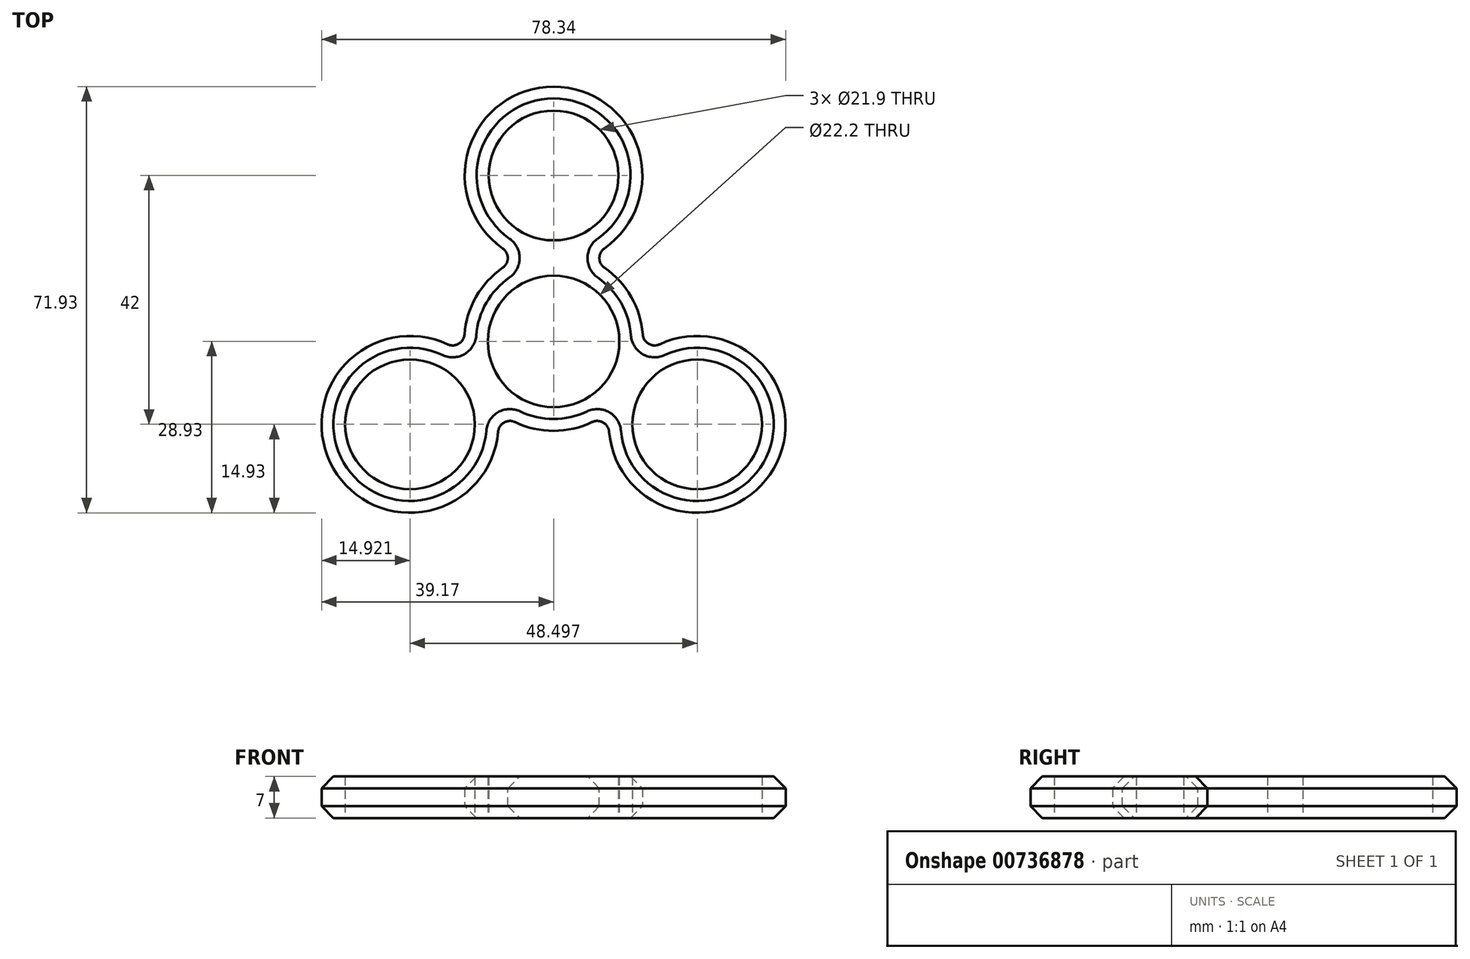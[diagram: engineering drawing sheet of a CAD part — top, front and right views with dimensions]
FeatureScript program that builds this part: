
annotation { "Feature Type Name" : "Feature", "Feature Type Description" : "" }
export const myFeature = defineFeature(function(context is Context, id is Id, definition is map)
    precondition{}
    {
        {
            var Q0;
            Q0=qCreatedBy(makeId("Top.planeOp"),FACE);
            var sketch = newSketch(context, id + "F0", { "sketchPlane" : qUnion([Q0])});
            skLineSegment(sketch, "E0", {"start": v(0, 0) * mm, "end": v(0, 28) * mm, "construction": true});
            skCircle(sketch, "E1", {"center": v(0, 28) * mm, "radius": 10.95 * mm});
            skArc(sketch, "E2", {"start": v(5.52, 14.05) * mm, "mid": v(0, 43) * mm, "end": v(-5.52, 14.05) * mm});
            skCircle(sketch, "E3", {"center": v(0, 0) * mm, "radius": 11.1 * mm});
            skArc(sketch, "E4", {"start": v(-9.5, -11.74) * mm, "mid": v(0, -15.1) * mm, "end": v(9.5, -11.74) * mm});
            skArc(sketch, "E5.1.2", {"start": v(-14.92, -2.35) * mm, "mid": v(-37.17, -21.46) * mm, "end": v(-9.5, -11.74) * mm});
            skCircle(sketch, "E5.1.3", {"center": v(-24.25, -14) * mm, "radius": 10.95 * mm});
            skArc(sketch, "E5.2.2", {"start": v(9.5, -11.74) * mm, "mid": v(37.17, -21.46) * mm, "end": v(14.92, -2.35) * mm});
            skCircle(sketch, "E5.2.3", {"center": v(24.25, -14) * mm, "radius": 10.95 * mm});
            skArc(sketch, "E6.trimOffspring", {"start": v(14.92, -2.35) * mm, "mid": v(13.1, 7.5) * mm, "end": v(5.52, 14.05) * mm});
            skArc(sketch, "E7.trimOffspring", {"start": v(-5.52, 14.05) * mm, "mid": v(-13.1, 7.5) * mm, "end": v(-14.92, -2.35) * mm});
            skLineSegment(sketch, "E8", {"start": v(0, 0) * mm, "end": v(-24.25, -14) * mm, "construction": true});
            skLineSegment(sketch, "E9", {"start": v(0, 0) * mm, "end": v(24.25, -14) * mm, "construction": true});
            skSolve(sketch);
        }
        {
            var Q0;
            Q0=qSketchRegion(id+"F0",true);
            extrude(context, id + "F1", {"entities" : qUnion([Q0]), "depth" : 7 * mm, "offsetDistance" : 25 * mm});
        }
        {
            var Q0;
            Q0=makeQuery(id+"F1.opExtrude","SWEPT_EDGE",EDGE,{"disambiguationData":[OSD([sQuery(id+"F0.wireOp",EDGE,"E4"),sQuery(id+"F0.wireOp",EDGE,"E5.1.2")])]});
            var Q1;
            Q1=makeQuery(id+"F1.opExtrude","SWEPT_EDGE",EDGE,{"disambiguationData":[OSD([sQuery(id+"F0.wireOp",EDGE,"E4"),sQuery(id+"F0.wireOp",EDGE,"E5.2.2")])]});
            var Q2;
            Q2=makeQuery(id+"F1.opExtrude","SWEPT_EDGE",EDGE,{"disambiguationData":[OSD([sQuery(id+"F0.wireOp",EDGE,"E5.2.2"),sQuery(id+"F0.wireOp",EDGE,"E6.trimOffspring")])]});
            var Q3;
            Q3=makeQuery(id+"F1.opExtrude","SWEPT_EDGE",EDGE,{"disambiguationData":[OSD([sQuery(id+"F0.wireOp",EDGE,"E2"),sQuery(id+"F0.wireOp",EDGE,"E6.trimOffspring")])]});
            var Q4;
            Q4=makeQuery(id+"F1.opExtrude","SWEPT_EDGE",EDGE,{"disambiguationData":[OSD([sQuery(id+"F0.wireOp",EDGE,"E2"),sQuery(id+"F0.wireOp",EDGE,"E7.trimOffspring")])]});
            var Q5;
            Q5=makeQuery(id+"F1.opExtrude","SWEPT_EDGE",EDGE,{"disambiguationData":[OSD([sQuery(id+"F0.wireOp",EDGE,"E5.1.2"),sQuery(id+"F0.wireOp",EDGE,"E7.trimOffspring")])]});
            fillet(context, id + "F2", {"entities" : qUnion([Q0, Q1, Q2, Q3, Q4, Q5]), "radius" : 2 * mm, "tangentPropagation" : true, "allowEdgeOverflow" : false});
        }
        {
            var Q0;
            Q0=makeQuery(id+"F1.opExtrude","CAP_EDGE",EDGE,{"disambiguationData":[OSD([sQuery(id+"F0.wireOp",EDGE,"E5.2.2")])],"isStart":true});
            var Q1;
            Q1=makeQuery(id+"F1.opExtrude","CAP_EDGE",EDGE,{"disambiguationData":[OSD([sQuery(id+"F0.wireOp",EDGE,"E5.2.2")])],"isStart":false});
            chamfer(context, id + "F3", {"entities" : qUnion([Q0, Q1]), "width" : 2 * mm, "tangentPropagation" : true});
        }
    });
